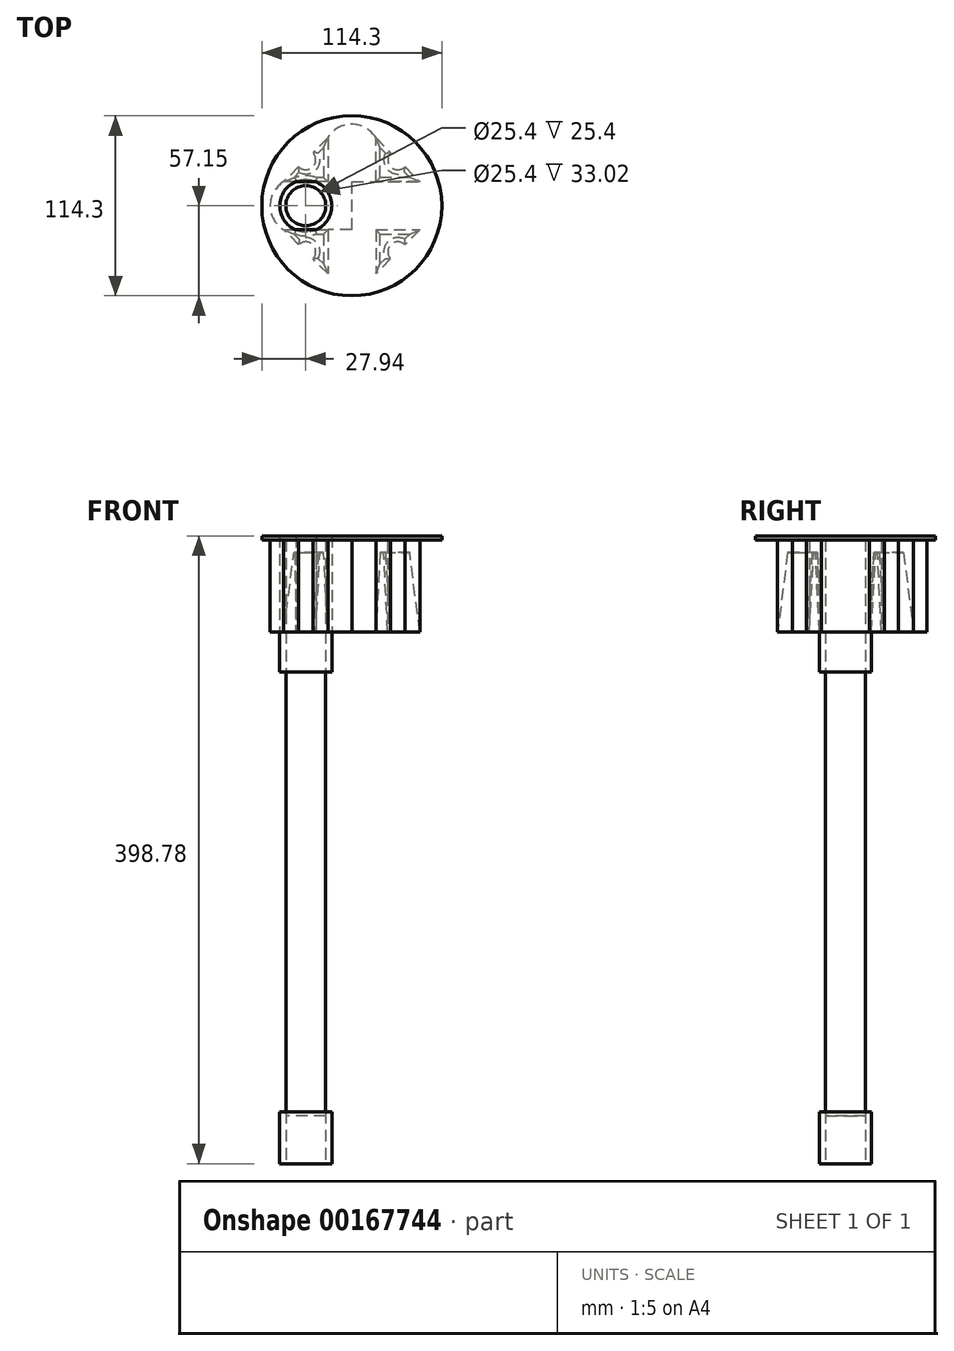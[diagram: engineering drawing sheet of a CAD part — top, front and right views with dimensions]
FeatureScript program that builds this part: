
annotation { "Feature Type Name" : "Feature", "Feature Type Description" : "" }
export const myFeature = defineFeature(function(context is Context, id is Id, definition is map)
    precondition{}
    {
        {
            var Q0;
            Q0=qCreatedBy(makeId("Top.planeOp"),FACE);
            var sketch = newSketch(context, id + "F0", { "sketchPlane" : qUnion([Q0])});
            skCircle(sketch, "E0", {"center": v(-29.21, 0) * mm, "radius": 16.51 * mm});
            skCircle(sketch, "E1", {"center": v(-29.21, 0) * mm, "radius": 12.7 * mm});
            skCircle(sketch, "E2.MirrorC", {"center": v(29.21, 0) * mm, "radius": 16.51 * mm});
            skCircle(sketch, "E3.MirrorC", {"center": v(29.21, 0) * mm, "radius": 12.7 * mm});
            skSolve(sketch);
        }
        {
            var Q0;
            Q0=makeQuery(id+"F0.imprint","IMPRINT",FACE,{"disambiguationData":[TD([[makeQuery(id+"F0.imprint","IMPRINT",EDGE,{"derivedFrom":sQuery(id+"F0.wireOp",EDGE,"E2.MirrorC")}),-1.0]])]});
            var Q1;
            Q1=makeQuery(id+"F0.imprint","IMPRINT",FACE,{"disambiguationData":[TD([[makeQuery(id+"F0.imprint","IMPRINT",EDGE,{"derivedFrom":sQuery(id+"F0.wireOp",EDGE,"E0")}),1.0]])]});
            extrude(context, id + "F1", {"entities" : qUnion([Q0, Q1]), "depth" : 33.02 * mm});
        }
        {
            var Q0;
            Q0=makeQuery(id+"F1.opExtrude","CAP_FACE",FACE,{"disambiguationData":[OSD([sQuery(id+"F0.wireOp",EDGE,"E0"),sQuery(id+"F0.wireOp",EDGE,"E1")])],"isStart":false});
            var sketch = newSketch(context, id + "F2", { "sketchPlane" : qUnion([Q0])});
            skSolve(sketch);
        }
        {
            var Q0;
            Q0=makeQuery(id+"F1.opExtrude","CAP_FACE",FACE,{"disambiguationData":[OSD([sQuery(id+"F0.wireOp",EDGE,"E2.MirrorC"),sQuery(id+"F0.wireOp",EDGE,"E3.MirrorC")])],"isStart":false});
            var sketch = newSketch(context, id + "F3", { "sketchPlane" : qUnion([Q0])});
            skSolve(sketch);
        }
        {
            var Q0;
            Q0=makeQuery(id+"F3.imprint","IMPRINT",FACE,{"disambiguationData":[TD([[makeQuery(id+"F3.imprint","IMPRINT",EDGE,{"derivedFrom":makeQuery(id+"F1.opExtrude","CAP_EDGE",EDGE,{"disambiguationData":[OSD([sQuery(id+"F0.wireOp",EDGE,"E3.MirrorC")])],"isStart":false})}),-1.0]])]});
            var Q1;
            Q1=makeQuery(id+"F2.imprint","IMPRINT",FACE,{"disambiguationData":[TD([[makeQuery(id+"F2.imprint","IMPRINT",EDGE,{"derivedFrom":makeQuery(id+"F1.opExtrude","CAP_EDGE",EDGE,{"disambiguationData":[OSD([sQuery(id+"F0.wireOp",EDGE,"E1")])],"isStart":false})}),1.0]])]});
            extrude(context, id + "F4", {"entities" : qUnion([Q0, Q1]), "depth" : 279.4 * mm, "hasSecondDirection" : true, "secondDirectionOppositeDirection" : true, "secondDirectionDepth" : 2.54 * mm});
        }
        {
            var Q0;
            Q0=makeQuery(id+"F4.opExtrude","CAP_FACE",FACE,{"disambiguationData":[OSD([sQuery(id+"F0.wireOp",EDGE,"E1")])],"isStart":false});
            var sketch = newSketch(context, id + "F5", { "sketchPlane" : qUnion([Q0])});
            skCircle(sketch, "E4", {"center": v(-29.21, 0) * mm, "radius": 16.51 * mm});
            skCircle(sketch, "E5", {"center": v(-29.21, 0) * mm, "radius": 12.7 * mm});
            skCircle(sketch, "E6.MirrorC", {"center": v(29.21, 0) * mm, "radius": 16.51 * mm});
            skCircle(sketch, "E7.MirrorC", {"center": v(29.21, 0) * mm, "radius": 12.7 * mm});
            skSolve(sketch);
        }
        {
            var Q0;
            Q0=makeQuery(id+"F5.imprint","IMPRINT",FACE,{"disambiguationData":[TD([[makeQuery(id+"F5.imprint","IMPRINT",EDGE,{"derivedFrom":sQuery(id+"F5.wireOp",EDGE,"E4")}),1.0]])]});
            var Q1;
            Q1=makeQuery(id+"F5.imprint","IMPRINT",FACE,{"disambiguationData":[TD([[makeQuery(id+"F5.imprint","IMPRINT",EDGE,{"derivedFrom":sQuery(id+"F5.wireOp",EDGE,"E6.MirrorC")}),-1.0]])]});
            extrude(context, id + "F6", {"entities" : qUnion([Q0, Q1]), "depth" : 25.4 * mm});
        }
        {
            var Q0;
            Q0=makeQuery(id+"F6.opExtrude","CAP_FACE",FACE,{"disambiguationData":[OSD([sQuery(id+"F5.wireOp",EDGE,"E4"),sQuery(id+"F5.wireOp",EDGE,"E5")])],"isStart":false});
            var sketch = newSketch(context, id + "F7", { "sketchPlane" : qUnion([Q0])});
            skLineSegment(sketch, "E8", {"start": v(0, 0) * mm, "end": v(0, 50.8) * mm});
            skLineSegment(sketch, "E9.MirrorCS", {"start": v(0, 0) * mm, "end": v(0, -50.8) * mm});
            skLineSegment(sketch, "E10", {"start": v(0, 0) * mm, "end": v(-50.8, 0) * mm});
            skLineSegment(sketch, "E11.MirrorCS", {"start": v(0, 0) * mm, "end": v(50.8, 0) * mm});
            skLineSegment(sketch, "E12", {"start": v(0, 0) * mm, "end": v(-15.24, 0) * mm});
            skLineSegment(sketch, "E13", {"start": v(0, 0) * mm, "end": v(0, 15.24) * mm});
            skLineSegment(sketch, "E14.MirrorCS", {"start": v(0, 0) * mm, "end": v(15.24, 0) * mm});
            skLineSegment(sketch, "E15.MirrorCS", {"start": v(0, 0) * mm, "end": v(0, -15.24) * mm});
            skLineSegment(sketch, "E16", {"start": v(-15.24, 0) * mm, "end": v(-15.24, 43.18) * mm});
            skLineSegment(sketch, "E17", {"start": v(0, 15.24) * mm, "end": v(-43.18, 15.24) * mm});
            skLineSegment(sketch, "E18.MirrorCS", {"start": v(15.24, 0) * mm, "end": v(15.24, 43.18) * mm});
            skLineSegment(sketch, "E19.MirrorCS", {"start": v(0, 15.24) * mm, "end": v(43.18, 15.24) * mm});
            skLineSegment(sketch, "E20.MirrorCS", {"start": v(-15.24, 0) * mm, "end": v(-15.24, -43.18) * mm});
            skLineSegment(sketch, "E21.MirrorCS", {"start": v(0, -15.24) * mm, "end": v(-43.18, -15.24) * mm});
            skLineSegment(sketch, "E22.MirrorCS", {"start": v(0, -15.24) * mm, "end": v(43.18, -15.24) * mm});
            skLineSegment(sketch, "E23.MirrorCS", {"start": v(15.24, 0) * mm, "end": v(15.24, -43.18) * mm});
            skArc(sketch, "E24", {"start": v(15.24, 43.18) * mm, "mid": v(0, 51.8) * mm, "end": v(-15.24, 43.18) * mm});
            skArc(sketch, "E25.MirrorCS", {"start": v(15.24, -43.18) * mm, "mid": v(0, -51.8) * mm, "end": v(-15.24, -43.18) * mm});
            skArc(sketch, "E26", {"start": v(-43.18, 15.24) * mm, "mid": v(-51.8, 0) * mm, "end": v(-43.18, -15.24) * mm});
            skArc(sketch, "E27.MirrorCS", {"start": v(43.18, 15.24) * mm, "mid": v(51.8, 0) * mm, "end": v(43.18, -15.24) * mm});
            skLineSegment(sketch, "E28", {"start": v(-15.24, 43.18) * mm, "end": v(-43.18, 15.24) * mm});
            skLineSegment(sketch, "E29", {"start": v(15.24, 43.18) * mm, "end": v(43.18, 15.24) * mm});
            skLineSegment(sketch, "E30", {"start": v(43.18, -15.24) * mm, "end": v(15.24, -43.18) * mm});
            skLineSegment(sketch, "E31", {"start": v(-15.24, -43.18) * mm, "end": v(-43.18, -15.24) * mm});
            skCircle(sketch, "E32", {"center": v(-29.21, 29.21) * mm, "radius": 6.35 * mm});
            skCircle(sketch, "E33", {"center": v(29.21, 29.21) * mm, "radius": 6.35 * mm});
            skCircle(sketch, "E34", {"center": v(29.21, -29.21) * mm, "radius": 6.35 * mm});
            skCircle(sketch, "E35", {"center": v(-29.21, -29.21) * mm, "radius": 6.35 * mm});
            skSolve(sketch);
        }
        {
            var Q0;
            {var subQ0=sQuery(id+"F7.wireOp",EDGE,"E32");var subQ1=sQuery(id+"F7.wireOp",EDGE,"E28");var subQ2=makeQuery(id+"F7.imprint","INTERSECT",VERTEX,{"disambiguationData":[OD(0.0)],"derivedFrom":[subQ1,subQ0]});Q0=makeQuery(id+"F7.imprint","IMPRINT",FACE,{"disambiguationData":[TD([[makeQuery(id+"F7.imprint","IMPRINT",EDGE,{"disambiguationData":[TD([[subQ2,-1.0]])],"derivedFrom":subQ1}),1.0]])]});}
            var Q1;
            {var subQ0=sQuery(id+"F7.wireOp",EDGE,"E33");var subQ1=sQuery(id+"F7.wireOp",EDGE,"E29");var subQ2=makeQuery(id+"F7.imprint","INTERSECT",VERTEX,{"disambiguationData":[OD(0.0)],"derivedFrom":[subQ1,subQ0]});Q1=makeQuery(id+"F7.imprint","IMPRINT",FACE,{"disambiguationData":[TD([[makeQuery(id+"F7.imprint","IMPRINT",EDGE,{"disambiguationData":[TD([[subQ2,-1.0]])],"derivedFrom":subQ1}),-1.0]])]});}
            var Q2;
            {var subQ0=sQuery(id+"F7.wireOp",EDGE,"E34");var subQ1=sQuery(id+"F7.wireOp",EDGE,"E30");var subQ2=makeQuery(id+"F7.imprint","INTERSECT",VERTEX,{"disambiguationData":[OD(0.0)],"derivedFrom":[subQ1,subQ0]});Q2=makeQuery(id+"F7.imprint","IMPRINT",FACE,{"disambiguationData":[TD([[makeQuery(id+"F7.imprint","IMPRINT",EDGE,{"disambiguationData":[TD([[subQ2,-1.0]])],"derivedFrom":subQ1}),-1.0]])]});}
            var Q3;
            {var subQ0=sQuery(id+"F7.wireOp",EDGE,"E35");var subQ1=sQuery(id+"F7.wireOp",EDGE,"E31");var subQ2=makeQuery(id+"F7.imprint","INTERSECT",VERTEX,{"disambiguationData":[OD(0.0)],"derivedFrom":[subQ1,subQ0]});Q3=makeQuery(id+"F7.imprint","IMPRINT",FACE,{"disambiguationData":[TD([[makeQuery(id+"F7.imprint","IMPRINT",EDGE,{"disambiguationData":[TD([[subQ2,-1.0]])],"derivedFrom":subQ1}),-1.0]])]});}
            var Q4;
            {var subQ0=sQuery(id+"F7.wireOp",EDGE,"E29");var subQ3=sQuery(id+"F7.wireOp",EDGE,"E33");var subQ4=makeQuery(id+"F7.imprint","INTERSECT",VERTEX,{"disambiguationData":[OD(0.0)],"derivedFrom":[subQ0,subQ3]});Q4=makeQuery(id+"F7.imprint","IMPRINT",FACE,{"disambiguationData":[TD([[makeQuery(id+"F7.imprint","IMPRINT",EDGE,{"disambiguationData":[TD([[subQ4,-1.0]])],"derivedFrom":subQ3}),-1.0]])]});}
            var Q5;
            {var subQ0=sQuery(id+"F7.wireOp",EDGE,"E30");var subQ3=sQuery(id+"F7.wireOp",EDGE,"E34");var subQ7=makeQuery(id+"F7.imprint","INTERSECT",VERTEX,{"disambiguationData":[OD(0.0)],"derivedFrom":[subQ0,subQ3]});Q5=makeQuery(id+"F7.imprint","IMPRINT",FACE,{"disambiguationData":[TD([[makeQuery(id+"F7.imprint","IMPRINT",EDGE,{"disambiguationData":[TD([[subQ7,-1.0]])],"derivedFrom":subQ3}),-1.0]])]});}
            var Q6;
            {var subQ7=sQuery(id+"F7.wireOp",EDGE,"E24");Q6=makeQuery(id+"F7.imprint","IMPRINT",FACE,{"disambiguationData":[TD([[makeQuery(id+"F7.imprint","IMPRINT",EDGE,{"derivedFrom":subQ7}),1.0]])]});}
            var Q7;
            {var subQ5=sQuery(id+"F7.wireOp",EDGE,"E27.MirrorCS");Q7=makeQuery(id+"F7.imprint","IMPRINT",FACE,{"disambiguationData":[TD([[makeQuery(id+"F7.imprint","IMPRINT",EDGE,{"derivedFrom":subQ5}),-1.0]])]});}
            var Q8;
            {var subQ0=sQuery(id+"F7.wireOp",EDGE,"E25.MirrorCS");Q8=makeQuery(id+"F7.imprint","IMPRINT",FACE,{"disambiguationData":[TD([[makeQuery(id+"F7.imprint","IMPRINT",EDGE,{"derivedFrom":subQ0}),-1.0]])]});}
            var Q9;
            {var subQ0=sQuery(id+"F7.wireOp",EDGE,"E17");var subQ1=makeQuery(id+"F6.opExtrude","CAP_EDGE",EDGE,{"disambiguationData":[OSD([sQuery(id+"F5.wireOp",EDGE,"E4")])],"isStart":false});var subQ2=makeQuery(id+"F7.imprint","INTERSECT",VERTEX,{"disambiguationData":[OD(0.0)],"derivedFrom":[subQ1,subQ0]});Q9=makeQuery(id+"F7.imprint","IMPRINT",FACE,{"disambiguationData":[TD([[makeQuery(id+"F7.imprint","IMPRINT",EDGE,{"disambiguationData":[TD([[subQ2,-1.0]])],"derivedFrom":subQ0}),-1.0]])]});}
            var Q10;
            {var subQ0=sQuery(id+"F7.wireOp",EDGE,"E21.MirrorCS");var subQ1=makeQuery(id+"F6.opExtrude","CAP_EDGE",EDGE,{"disambiguationData":[OSD([sQuery(id+"F5.wireOp",EDGE,"E4")])],"isStart":false});var subQ2=makeQuery(id+"F7.imprint","INTERSECT",VERTEX,{"disambiguationData":[OD(0.0)],"derivedFrom":[subQ1,subQ0]});Q10=makeQuery(id+"F7.imprint","IMPRINT",FACE,{"disambiguationData":[TD([[makeQuery(id+"F7.imprint","IMPRINT",EDGE,{"disambiguationData":[TD([[subQ2,-1.0]])],"derivedFrom":subQ0}),1.0]])]});}
            var Q11;
            {var subQ0=sQuery(id+"F7.wireOp",EDGE,"E17");var subQ1=sQuery(id+"F7.wireOp",EDGE,"E16");var subQ2=makeQuery(id+"F7.imprint","INTERSECT",VERTEX,{"derivedFrom":[subQ1,subQ0]});Q11=makeQuery(id+"F7.imprint","IMPRINT",FACE,{"disambiguationData":[TD([[makeQuery(id+"F7.imprint","IMPRINT",EDGE,{"disambiguationData":[TD([[subQ2,1.0]])],"derivedFrom":subQ1}),1.0]])]});}
            var Q12;
            {var subQ0=sQuery(id+"F7.wireOp",EDGE,"E21.MirrorCS");var subQ1=sQuery(id+"F7.wireOp",EDGE,"E20.MirrorCS");var subQ2=makeQuery(id+"F7.imprint","INTERSECT",VERTEX,{"derivedFrom":[subQ1,subQ0]});Q12=makeQuery(id+"F7.imprint","IMPRINT",FACE,{"disambiguationData":[TD([[makeQuery(id+"F7.imprint","IMPRINT",EDGE,{"disambiguationData":[TD([[subQ2,1.0]])],"derivedFrom":subQ1}),-1.0]])]});}
            var Q13;
            {var subQ1=sQuery(id+"F7.wireOp",EDGE,"E16");var subQ5=sQuery(id+"F7.wireOp",EDGE,"E17");var subQ6=makeQuery(id+"F7.imprint","INTERSECT",VERTEX,{"derivedFrom":[subQ1,subQ5]});Q13=makeQuery(id+"F7.imprint","IMPRINT",FACE,{"disambiguationData":[TD([[makeQuery(id+"F7.imprint","IMPRINT",EDGE,{"disambiguationData":[TD([[subQ6,-1.0]])],"derivedFrom":subQ5}),-1.0]])]});}
            var Q14;
            {var subQ1=sQuery(id+"F7.wireOp",EDGE,"E20.MirrorCS");var subQ5=sQuery(id+"F7.wireOp",EDGE,"E21.MirrorCS");var subQ6=makeQuery(id+"F7.imprint","INTERSECT",VERTEX,{"derivedFrom":[subQ1,subQ5]});Q14=makeQuery(id+"F7.imprint","IMPRINT",FACE,{"disambiguationData":[TD([[makeQuery(id+"F7.imprint","IMPRINT",EDGE,{"disambiguationData":[TD([[subQ6,-1.0]])],"derivedFrom":subQ5}),1.0]])]});}
            var Q15;
            {var subQ4=sQuery(id+"F7.wireOp",EDGE,"E26");Q15=makeQuery(id+"F7.imprint","IMPRINT",FACE,{"disambiguationData":[TD([[makeQuery(id+"F7.imprint","IMPRINT",EDGE,{"derivedFrom":subQ4}),1.0]])]});}
            var Q16;
            {var subQ1=sQuery(id+"F7.wireOp",EDGE,"E10");var subQ3=makeQuery(id+"F6.opExtrude","CAP_EDGE",EDGE,{"disambiguationData":[OSD([sQuery(id+"F5.wireOp",EDGE,"E4")])],"isStart":false});var subQ8=makeQuery(id+"F7.imprint","INTERSECT",VERTEX,{"derivedFrom":[subQ3,subQ1]});Q16=makeQuery(id+"F7.imprint","IMPRINT",FACE,{"disambiguationData":[TD([[makeQuery(id+"F7.imprint","IMPRINT",EDGE,{"disambiguationData":[TD([[subQ8,1.0]])],"derivedFrom":subQ1}),-1.0]])]});}
            var Q17;
            {var subQ1=makeQuery(id+"F6.opExtrude","CAP_EDGE",EDGE,{"disambiguationData":[OSD([sQuery(id+"F5.wireOp",EDGE,"E4")])],"isStart":false});var subQ4=sQuery(id+"F7.wireOp",EDGE,"E10");var subQ11=makeQuery(id+"F7.imprint","INTERSECT",VERTEX,{"derivedFrom":[subQ1,subQ4]});Q17=makeQuery(id+"F7.imprint","IMPRINT",FACE,{"disambiguationData":[TD([[makeQuery(id+"F7.imprint","IMPRINT",EDGE,{"disambiguationData":[TD([[subQ11,1.0]])],"derivedFrom":subQ4}),1.0]])]});}
            var Q18;
            {var subQ0=sQuery(id+"F7.wireOp",EDGE,"E10");var subQ1=makeQuery(id+"F6.opExtrude","CAP_EDGE",EDGE,{"disambiguationData":[OSD([sQuery(id+"F5.wireOp",EDGE,"E5")])],"isStart":false});var subQ2=makeQuery(id+"F7.imprint","INTERSECT",VERTEX,{"disambiguationData":[OD(0.0)],"derivedFrom":[subQ1,subQ0]});Q18=makeQuery(id+"F7.imprint","IMPRINT",FACE,{"disambiguationData":[TD([[makeQuery(id+"F7.imprint","IMPRINT",EDGE,{"disambiguationData":[TD([[subQ2,-1.0]])],"derivedFrom":subQ0}),-1.0]])]});}
            var Q19;
            {var subQ0=sQuery(id+"F7.wireOp",EDGE,"E10");var subQ1=makeQuery(id+"F6.opExtrude","CAP_EDGE",EDGE,{"disambiguationData":[OSD([sQuery(id+"F5.wireOp",EDGE,"E5")])],"isStart":false});var subQ2=makeQuery(id+"F7.imprint","INTERSECT",VERTEX,{"disambiguationData":[OD(0.0)],"derivedFrom":[subQ1,subQ0]});Q19=makeQuery(id+"F7.imprint","IMPRINT",FACE,{"disambiguationData":[TD([[makeQuery(id+"F7.imprint","IMPRINT",EDGE,{"disambiguationData":[TD([[subQ2,-1.0]])],"derivedFrom":subQ0}),1.0]])]});}
            var Q20;
            {var subQ0=sQuery(id+"F7.wireOp",EDGE,"E13");Q20=makeQuery(id+"F7.imprint","IMPRINT",FACE,{"disambiguationData":[TD([[makeQuery(id+"F7.imprint","IMPRINT",EDGE,{"derivedFrom":subQ0}),-1.0]])]});}
            var Q21;
            {var subQ0=sQuery(id+"F7.wireOp",EDGE,"E14.MirrorCS");Q21=makeQuery(id+"F7.imprint","IMPRINT",FACE,{"disambiguationData":[TD([[makeQuery(id+"F7.imprint","IMPRINT",EDGE,{"derivedFrom":subQ0}),-1.0]])]});}
            var Q22;
            {var subQ1=sQuery(id+"F7.wireOp",EDGE,"E15.MirrorCS");Q22=makeQuery(id+"F7.imprint","IMPRINT",FACE,{"disambiguationData":[TD([[makeQuery(id+"F7.imprint","IMPRINT",EDGE,{"derivedFrom":subQ1}),-1.0]])]});}
            var Q23;
            {var subQ5=sQuery(id+"F7.wireOp",EDGE,"E13");Q23=makeQuery(id+"F7.imprint","IMPRINT",FACE,{"disambiguationData":[TD([[makeQuery(id+"F7.imprint","IMPRINT",EDGE,{"derivedFrom":subQ5}),1.0]])]});}
            var Q24;
            {var subQ1=sQuery(id+"F7.wireOp",EDGE,"E12");var subQ3=makeQuery(id+"F6.opExtrude","CAP_EDGE",EDGE,{"disambiguationData":[OSD([sQuery(id+"F5.wireOp",EDGE,"E4")])],"isStart":false});var subQ4=makeQuery(id+"F7.imprint","INTERSECT",VERTEX,{"derivedFrom":[subQ3,subQ1]});Q24=makeQuery(id+"F7.imprint","IMPRINT",FACE,{"disambiguationData":[TD([[makeQuery(id+"F7.imprint","IMPRINT",EDGE,{"disambiguationData":[TD([[subQ4,-1.0]])],"derivedFrom":subQ3}),1.0]])]});}
            var Q25;
            {var subQ1=sQuery(id+"F7.wireOp",EDGE,"E12");var subQ3=makeQuery(id+"F6.opExtrude","CAP_EDGE",EDGE,{"disambiguationData":[OSD([sQuery(id+"F5.wireOp",EDGE,"E4")])],"isStart":false});var subQ4=makeQuery(id+"F7.imprint","INTERSECT",VERTEX,{"derivedFrom":[subQ3,subQ1]});Q25=makeQuery(id+"F7.imprint","IMPRINT",FACE,{"disambiguationData":[TD([[makeQuery(id+"F7.imprint","IMPRINT",EDGE,{"disambiguationData":[TD([[subQ4,1.0]])],"derivedFrom":subQ3}),1.0]])]});}
            extrude(context, id + "F8", {"entities" : qUnion([Q0, Q1, Q2, Q3, Q4, Q5, Q6, Q7, Q8, Q9, Q10, Q11, Q12, Q13, Q14, Q15, Q16, Q17, Q18, Q19, Q20, Q21, Q22, Q23, Q24, Q25]), "depth" : 58.42 * mm});
        }
        {
            var Q0;
            Q0=makeQuery(id+"F8.opExtrude","CAP_FACE",FACE,{"disambiguationData":[OSD([sQuery(id+"F7.wireOp",EDGE,"E24"),sQuery(id+"F7.wireOp",EDGE,"E25.MirrorCS"),sQuery(id+"F7.wireOp",EDGE,"E26"),sQuery(id+"F7.wireOp",EDGE,"E27.MirrorCS"),sQuery(id+"F7.wireOp",EDGE,"E28"),sQuery(id+"F7.wireOp",EDGE,"E29"),sQuery(id+"F7.wireOp",EDGE,"E30"),sQuery(id+"F7.wireOp",EDGE,"E31")])],"isStart":false});
            var sketch = newSketch(context, id + "F9", { "sketchPlane" : qUnion([Q0])});
            skCircle(sketch, "E36", {"center": v(0, 0) * mm, "radius": 57.15 * mm});
            skSolve(sketch);
        }
        {
            var Q0;
            {var subQ6=makeQuery(id+"F8.opExtrude","CAP_EDGE",EDGE,{"disambiguationData":[OSD([sQuery(id+"F7.wireOp",EDGE,"E28")])],"isStart":false});Q0=makeQuery(id+"F9.imprint","IMPRINT",FACE,{"disambiguationData":[TD([[makeQuery(id+"F9.imprint","IMPRINT",EDGE,{"derivedFrom":subQ6}),1.0]])]});}
            var Q1;
            {var subQ1=makeQuery(id+"F8.opExtrude","CAP_EDGE",EDGE,{"disambiguationData":[OSD([sQuery(id+"F7.wireOp",EDGE,"E30")])],"isStart":false});Q1=makeQuery(id+"F9.imprint","IMPRINT",FACE,{"disambiguationData":[TD([[makeQuery(id+"F9.imprint","IMPRINT",EDGE,{"derivedFrom":subQ1}),1.0]])]});}
            var Q2;
            {var subQ1=makeQuery(id+"F8.opExtrude","CAP_EDGE",EDGE,{"disambiguationData":[OSD([sQuery(id+"F7.wireOp",EDGE,"E28")])],"isStart":false});Q2=makeQuery(id+"F9.imprint","IMPRINT",FACE,{"disambiguationData":[TD([[makeQuery(id+"F9.imprint","IMPRINT",EDGE,{"derivedFrom":subQ1}),-1.0]])]});}
            var Q3;
            {var subQ1=makeQuery(id+"F8.opExtrude","CAP_EDGE",EDGE,{"disambiguationData":[OSD([sQuery(id+"F7.wireOp",EDGE,"E31")])],"isStart":false});Q3=makeQuery(id+"F9.imprint","IMPRINT",FACE,{"disambiguationData":[TD([[makeQuery(id+"F9.imprint","IMPRINT",EDGE,{"derivedFrom":subQ1}),1.0]])]});}
            var Q4;
            {var subQ1=makeQuery(id+"F8.opExtrude","CAP_EDGE",EDGE,{"disambiguationData":[OSD([sQuery(id+"F7.wireOp",EDGE,"E29")])],"isStart":false});Q4=makeQuery(id+"F9.imprint","IMPRINT",FACE,{"disambiguationData":[TD([[makeQuery(id+"F9.imprint","IMPRINT",EDGE,{"derivedFrom":subQ1}),1.0]])]});}
            extrude(context, id + "F10", {"entities" : qUnion([Q0, Q1, Q2, Q3, Q4]), "operationType" : NewBodyOperationType.ADD, "depth" : 2.54 * mm});
        }
        {
            var Q0;
            Q0=makeQuery(id+"F10.opExtrude","CAP_FACE",FACE,{"disambiguationData":[OSD([sQuery(id+"F9.wireOp",EDGE,"E36")])],"isStart":false});
            var sketch = newSketch(context, id + "F11", { "sketchPlane" : qUnion([Q0])});
            skLineSegment(sketch, "E37", {"start": v(0, -65.11) * mm, "end": v(0, 73.33) * mm});
            skLineSegment(sketch, "E38", {"start": v(-61.17, 51.26) * mm, "end": v(69.16, -58.1) * mm});
            skLineSegment(sketch, "E39", {"start": v(-34.08, 28.53) * mm, "end": v(-43.7, 17.08) * mm});
            skLineSegment(sketch, "E40", {"start": v(-24.35, 20.37) * mm, "end": v(-41.45, 0) * mm});
            skLineSegment(sketch, "E41", {"start": v(-14.63, 12.2) * mm, "end": v(-31.25, -7.6) * mm});
            skLineSegment(sketch, "E42", {"start": v(-4.9, 4.04) * mm, "end": v(-23.46, -18.08) * mm});
            skLineSegment(sketch, "E43", {"start": v(14.56, -12.28) * mm, "end": v(-5.04, -35.64) * mm});
            skLineSegment(sketch, "E44", {"start": v(4.83, -4.12) * mm, "end": v(-17.54, -30.78) * mm});
            skLineSegment(sketch, "E45", {"start": v(24.29, -20.45) * mm, "end": v(8.66, -39.07) * mm});
            skLineSegment(sketch, "E46", {"start": v(34.02, -28.61) * mm, "end": v(23.38, -41.29) * mm});
            skSolve(sketch);
        }
        {
            var Q0;
            Q0=sQuery(id+"F11.wireOp",EDGE,"E39");
            cPlane(context, id + "F12", {"entities" : qUnion([Q0]), "cplaneType" : CPlaneType.LINE_ANGLE, "offset" : 25.4 * mm, "angle" : 90 * degree, "width" : 152.4 * mm, "height" : 152.4 * mm});
        }
        {
            var Q0;
            Q0=sQuery(id+"F11.wireOp",EDGE,"E40");
            cPlane(context, id + "F13", {"entities" : qUnion([Q0]), "cplaneType" : CPlaneType.LINE_ANGLE, "offset" : 25.4 * mm, "angle" : 90 * degree, "width" : 152.4 * mm, "height" : 152.4 * mm});
        }
        {
            var Q0;
            Q0=sQuery(id+"F11.wireOp",EDGE,"E41");
            cPlane(context, id + "F14", {"entities" : qUnion([Q0]), "cplaneType" : CPlaneType.LINE_ANGLE, "offset" : 25.4 * mm, "angle" : 90 * degree, "width" : 152.4 * mm, "height" : 152.4 * mm});
        }
        {
            var Q0;
            {var subQ0=sQuery(id+"F7.wireOp",EDGE,"E32");var subQ1=sQuery(id+"F7.wireOp",EDGE,"E28");var subQ2=makeQuery(id+"F7.imprint","INTERSECT",VERTEX,{"disambiguationData":[OD(0.0)],"derivedFrom":[subQ1,subQ0]});Q0=makeQuery(id+"F7.imprint","IMPRINT",FACE,{"disambiguationData":[TD([[makeQuery(id+"F7.imprint","IMPRINT",EDGE,{"disambiguationData":[TD([[subQ2,-1.0]])],"derivedFrom":subQ1}),-1.0]])]});}
            var Q1;
            {var subQ0=sQuery(id+"F7.wireOp",EDGE,"E32");var subQ1=sQuery(id+"F7.wireOp",EDGE,"E28");var subQ2=makeQuery(id+"F7.imprint","INTERSECT",VERTEX,{"disambiguationData":[OD(0.0)],"derivedFrom":[subQ1,subQ0]});Q1=makeQuery(id+"F7.imprint","IMPRINT",FACE,{"disambiguationData":[TD([[makeQuery(id+"F7.imprint","IMPRINT",EDGE,{"disambiguationData":[TD([[subQ2,-1.0]])],"derivedFrom":subQ1}),1.0]])]});}
            var Q2;
            {var subQ0=sQuery(id+"F7.wireOp",EDGE,"E33");var subQ1=sQuery(id+"F7.wireOp",EDGE,"E29");var subQ2=makeQuery(id+"F7.imprint","INTERSECT",VERTEX,{"disambiguationData":[OD(0.0)],"derivedFrom":[subQ1,subQ0]});Q2=makeQuery(id+"F7.imprint","IMPRINT",FACE,{"disambiguationData":[TD([[makeQuery(id+"F7.imprint","IMPRINT",EDGE,{"disambiguationData":[TD([[subQ2,-1.0]])],"derivedFrom":subQ1}),-1.0]])]});}
            var Q3;
            {var subQ0=sQuery(id+"F7.wireOp",EDGE,"E33");var subQ1=sQuery(id+"F7.wireOp",EDGE,"E29");var subQ2=makeQuery(id+"F7.imprint","INTERSECT",VERTEX,{"disambiguationData":[OD(0.0)],"derivedFrom":[subQ1,subQ0]});Q3=makeQuery(id+"F7.imprint","IMPRINT",FACE,{"disambiguationData":[TD([[makeQuery(id+"F7.imprint","IMPRINT",EDGE,{"disambiguationData":[TD([[subQ2,-1.0]])],"derivedFrom":subQ1}),1.0]])]});}
            var Q4;
            {var subQ0=sQuery(id+"F7.wireOp",EDGE,"E35");var subQ1=sQuery(id+"F7.wireOp",EDGE,"E31");var subQ2=makeQuery(id+"F7.imprint","INTERSECT",VERTEX,{"disambiguationData":[OD(0.0)],"derivedFrom":[subQ1,subQ0]});Q4=makeQuery(id+"F7.imprint","IMPRINT",FACE,{"disambiguationData":[TD([[makeQuery(id+"F7.imprint","IMPRINT",EDGE,{"disambiguationData":[TD([[subQ2,-1.0]])],"derivedFrom":subQ1}),1.0]])]});}
            var Q5;
            {var subQ0=sQuery(id+"F7.wireOp",EDGE,"E35");var subQ1=sQuery(id+"F7.wireOp",EDGE,"E31");var subQ2=makeQuery(id+"F7.imprint","INTERSECT",VERTEX,{"disambiguationData":[OD(0.0)],"derivedFrom":[subQ1,subQ0]});Q5=makeQuery(id+"F7.imprint","IMPRINT",FACE,{"disambiguationData":[TD([[makeQuery(id+"F7.imprint","IMPRINT",EDGE,{"disambiguationData":[TD([[subQ2,-1.0]])],"derivedFrom":subQ1}),-1.0]])]});}
            var Q6;
            {var subQ0=sQuery(id+"F7.wireOp",EDGE,"E34");var subQ1=sQuery(id+"F7.wireOp",EDGE,"E30");var subQ2=makeQuery(id+"F7.imprint","INTERSECT",VERTEX,{"disambiguationData":[OD(0.0)],"derivedFrom":[subQ1,subQ0]});Q6=makeQuery(id+"F7.imprint","IMPRINT",FACE,{"disambiguationData":[TD([[makeQuery(id+"F7.imprint","IMPRINT",EDGE,{"disambiguationData":[TD([[subQ2,-1.0]])],"derivedFrom":subQ1}),1.0]])]});}
            var Q7;
            {var subQ0=sQuery(id+"F7.wireOp",EDGE,"E34");var subQ1=sQuery(id+"F7.wireOp",EDGE,"E30");var subQ2=makeQuery(id+"F7.imprint","INTERSECT",VERTEX,{"disambiguationData":[OD(0.0)],"derivedFrom":[subQ1,subQ0]});Q7=makeQuery(id+"F7.imprint","IMPRINT",FACE,{"disambiguationData":[TD([[makeQuery(id+"F7.imprint","IMPRINT",EDGE,{"disambiguationData":[TD([[subQ2,-1.0]])],"derivedFrom":subQ1}),-1.0]])]});}
            extrude(context, id + "F15", {"entities" : qUnion([Q0, Q1, Q2, Q3, Q4, Q5, Q6, Q7]), "operationType" : NewBodyOperationType.REMOVE, "depth" : 50.3 * mm, "hasDraft" : true, "draftAngle" : 3 * degree, "draftPullDirection" : true});
        }
        {
            var Q0;
            Q0=sQuery(id+"F11.wireOp",EDGE,"E42");
            cPlane(context, id + "F16", {"entities" : qUnion([Q0]), "cplaneType" : CPlaneType.LINE_ANGLE, "offset" : 25.4 * mm, "angle" : 90 * degree, "width" : 152.4 * mm, "height" : 152.4 * mm});
        }
        {
            var Q0;
            Q0=sQuery(id+"F11.wireOp",EDGE,"E44");
            cPlane(context, id + "F17", {"entities" : qUnion([Q0]), "cplaneType" : CPlaneType.LINE_ANGLE, "offset" : 25.4 * mm, "angle" : 90 * degree, "width" : 152.4 * mm, "height" : 152.4 * mm});
        }
        {
            var Q0;
            Q0=sQuery(id+"F11.wireOp",EDGE,"E43");
            cPlane(context, id + "F18", {"entities" : qUnion([Q0]), "cplaneType" : CPlaneType.LINE_ANGLE, "offset" : 25.4 * mm, "angle" : 90 * degree, "width" : 152.4 * mm, "height" : 152.4 * mm});
        }
        {
            var Q0;
            Q0=sQuery(id+"F11.wireOp",EDGE,"E45");
            cPlane(context, id + "F19", {"entities" : qUnion([Q0]), "cplaneType" : CPlaneType.LINE_ANGLE, "offset" : 25.4 * mm, "angle" : 90 * degree, "width" : 152.4 * mm, "height" : 152.4 * mm});
        }
        {
            var Q0;
            Q0=sQuery(id+"F11.wireOp",EDGE,"E46");
            cPlane(context, id + "F20", {"entities" : qUnion([Q0]), "cplaneType" : CPlaneType.LINE_ANGLE, "offset" : 25.4 * mm, "angle" : 90 * degree, "width" : 152.4 * mm, "height" : 152.4 * mm});
        }
    });
